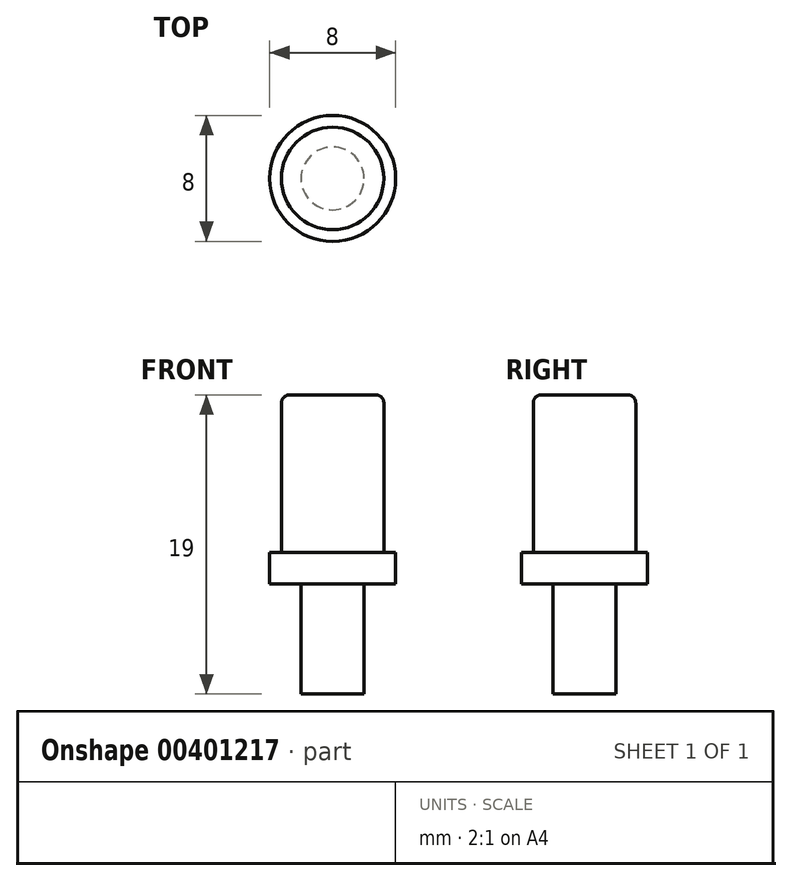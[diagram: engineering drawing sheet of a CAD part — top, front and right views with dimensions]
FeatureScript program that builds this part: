
annotation { "Feature Type Name" : "Feature", "Feature Type Description" : "" }
export const myFeature = defineFeature(function(context is Context, id is Id, definition is map)
    precondition{}
    {
        {
            var Q0;
            Q0=qCreatedBy(makeId("Top.planeOp"),FACE);
            var sketch = newSketch(context, id + "F0", { "sketchPlane" : qUnion([Q0])});
            skCircle(sketch, "E0", {"center": v(0, 0) * mm, "radius": 4 * mm});
            skCircle(sketch, "E1", {"center": v(0, 0) * mm, "radius": 2 * mm});
            skSolve(sketch);
        }
        {
            var Q0;
            Q0 = qSketchRegion(id + "F0", true);
            var Q1;
            Q1=makeQuery(id+"F0.imprint","IMPRINT",FACE,{"disambiguationData":[TD([[makeQuery(id+"F0.imprint","IMPRINT",EDGE,{"derivedFrom":sQuery(id+"F0.wireOp",EDGE,"E1")}),1.0]])]});
            extrude(context, id + "F1", {"entities" : qUnion([Q0, Q1]), "depth" : 2 * mm, "offsetDistance" : 25 * mm});
        }
        {
            var Q0;
            Q0=makeQuery(id+"F1.opExtrude","CAP_FACE",FACE,{"disambiguationData":[OSD([sQuery(id+"F0.wireOp",EDGE,"E0")])],"isStart":false});
            var sketch = newSketch(context, id + "F2", { "sketchPlane" : qUnion([Q0])});
            skCircle(sketch, "E2", {"center": v(0, 0) * mm, "radius": 3.25 * mm});
            skSolve(sketch);
        }
        {
            var Q0;
            Q0 = qSketchRegion(id + "F2", true);
            extrude(context, id + "F3", {"entities" : qUnion([Q0]), "operationType" : NewBodyOperationType.ADD, "depth" : 10 * mm, "offsetDistance" : 25 * mm});
        }
        {
            var Q0;
            Q0=makeQuery(id+"F0.imprint","IMPRINT",FACE,{"disambiguationData":[TD([[makeQuery(id+"F0.imprint","IMPRINT",EDGE,{"derivedFrom":sQuery(id+"F0.wireOp",EDGE,"E1")}),1.0]])]});
            extrude(context, id + "F4", {"entities" : qUnion([Q0]), "operationType" : NewBodyOperationType.ADD, "oppositeDirection" : true, "depth" : 7 * mm, "offsetDistance" : 25 * mm});
        }
        {
            var Q0;
            Q0=makeQuery(id+"F3.opExtrude","CAP_EDGE",EDGE,{"disambiguationData":[OSD([sQuery(id+"F2.wireOp",EDGE,"E2")])],"isStart":false});
            fillet(context, id + "F5", {"entities" : qUnion([Q0]), "tangentPropagation" : true, "radius" : 0.5 * mm, "defaultsChanged" : true, "vertexSettings" : [], "allowEdgeOverflow" : false});
        }
    });
